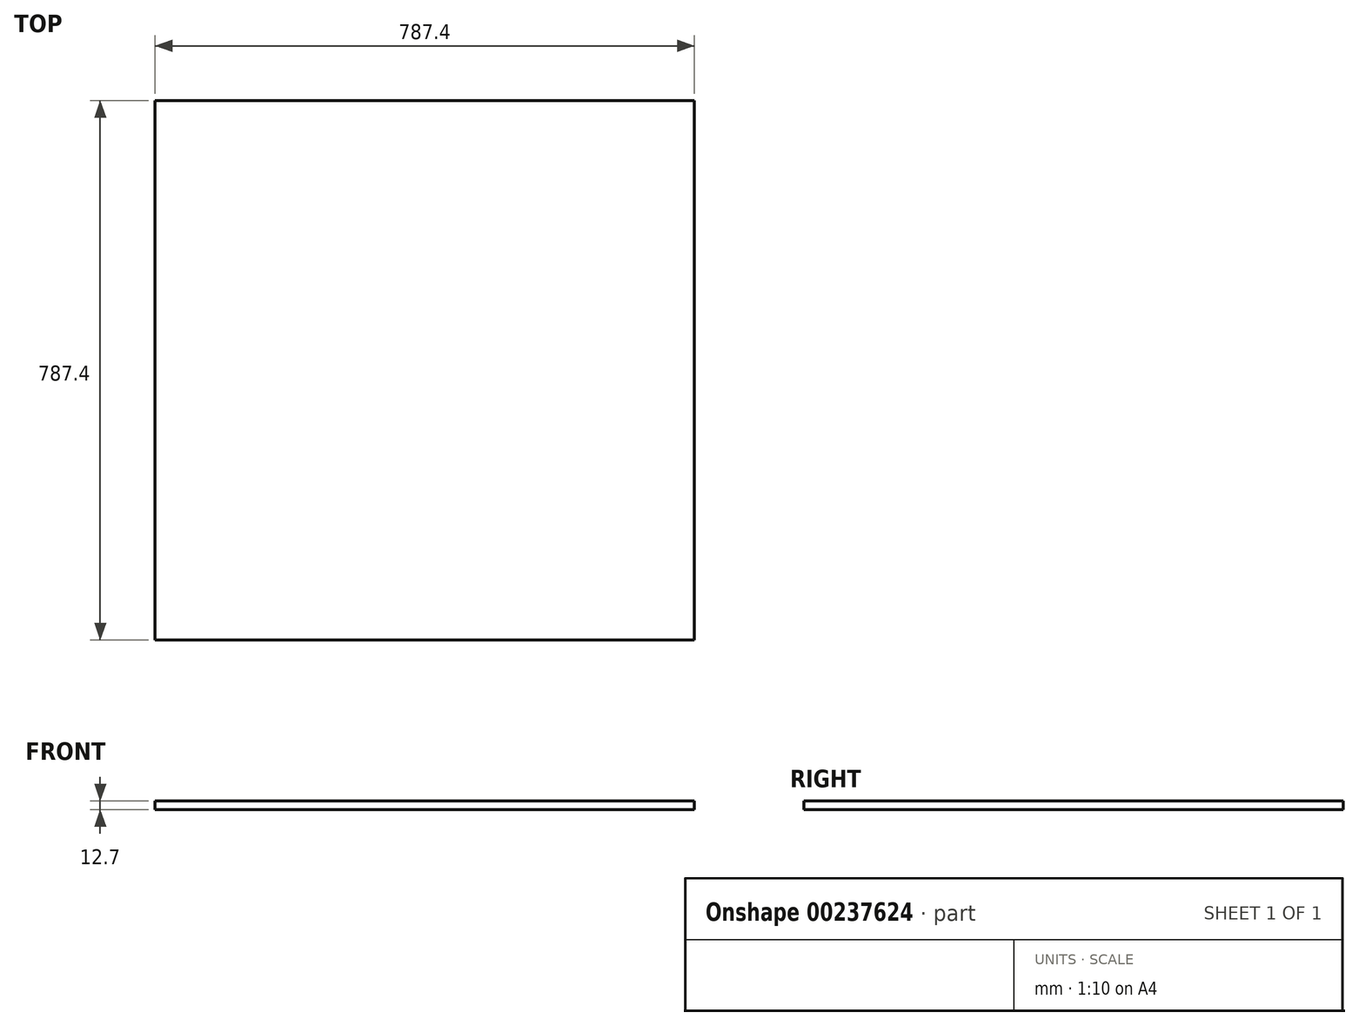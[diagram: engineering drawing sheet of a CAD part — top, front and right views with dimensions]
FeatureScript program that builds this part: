
annotation { "Feature Type Name" : "Feature", "Feature Type Description" : "" }
export const myFeature = defineFeature(function(context is Context, id is Id, definition is map)
    precondition{}
    {
        {
            var Q0;
            Q0=qCreatedBy(makeId("Top.planeOp"),FACE);
            var sketch = newSketch(context, id + "F0", { "sketchPlane" : qUnion([Q0])});
            skLineSegment(sketch, "E0.bottom", {"start": v(0, 0) * mm, "end": v(787.4, 0) * mm});
            skLineSegment(sketch, "E0.top", {"start": v(0, 787.4) * mm, "end": v(787.4, 787.4) * mm});
            skLineSegment(sketch, "E0.left", {"start": v(0, 0) * mm, "end": v(0, 787.4) * mm});
            skLineSegment(sketch, "E0.right", {"start": v(787.4, 0) * mm, "end": v(787.4, 787.4) * mm});
            skSolve(sketch);
        }
        {
            var Q0;
            Q0=makeQuery(id+"F0.imprint","IMPRINT",FACE,{"disambiguationData":[TD([[makeQuery(id+"F0.imprint","IMPRINT",EDGE,{"derivedFrom":sQuery(id+"F0.wireOp",EDGE,"E0.bottom")}),1.0]])]});
            extrude(context, id + "F1", {"entities" : qUnion([Q0]), "depth" : 12.7 * mm});
        }
    });
